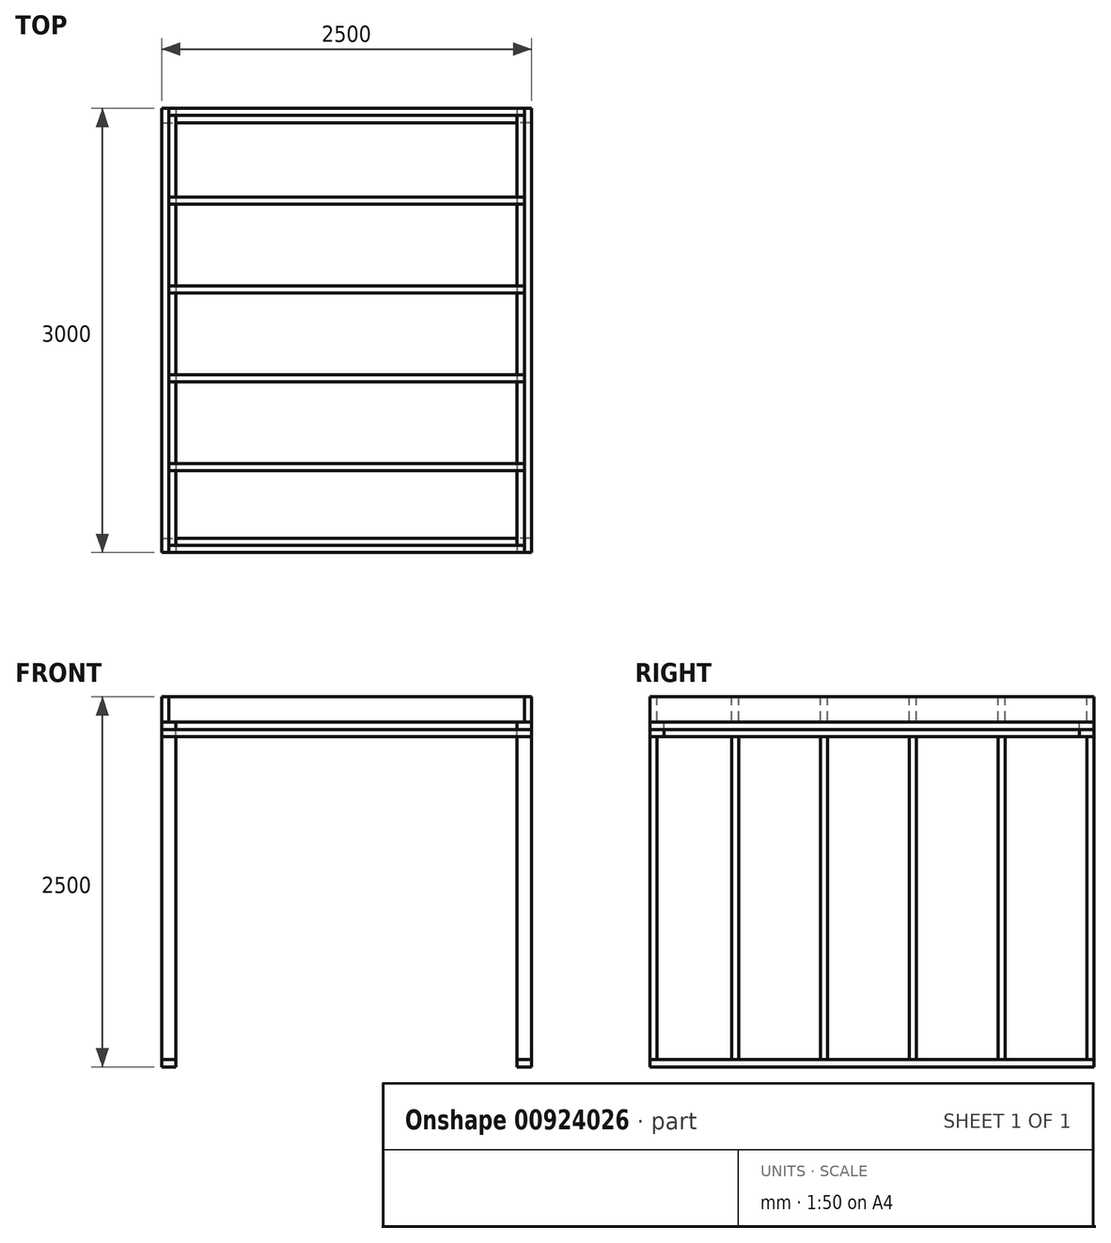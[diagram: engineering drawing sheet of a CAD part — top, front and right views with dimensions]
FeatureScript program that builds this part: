
annotation { "Feature Type Name" : "Feature", "Feature Type Description" : "" }
export const myFeature = defineFeature(function(context is Context, id is Id, definition is map)
    precondition{}
    {
        {
            assignVariable(context, id + "F0", {"name" : "poikkiparrun_korkeus", "anyValue" : 172});
        }
        {
            assignVariable(context, id + "F1", {"name" : "koolauspuun_paksuus", "anyValue" : 48});
        }
        {
            assignVariable(context, id + "F2", {"name" : "koolauspuun_korkeus", "anyValue" : 97});
        }
        {
            var Q0;
            Q0=qCreatedBy(makeId("Top.planeOp"),FACE);
            var sketch = newSketch(context, id + "F3", { "sketchPlane" : qUnion([Q0])});
            skLineSegment(sketch, "E0.bottom", {"start": v(0, 0) * mm, "end": v(-48, 0) * mm});
            skLineSegment(sketch, "E0.top", {"start": v(0, -3000) * mm, "end": v(-48, -3000) * mm});
            skLineSegment(sketch, "E0.left", {"start": v(0, 0) * mm, "end": v(0, -3000) * mm});
            skLineSegment(sketch, "E0.right", {"start": v(-48, 0) * mm, "end": v(-48, -3000) * mm});
            skLineSegment(sketch, "E1.bottom", {"start": v(-2452, 0) * mm, "end": v(-2500, 0) * mm});
            skLineSegment(sketch, "E1.top", {"start": v(-2452, -3000) * mm, "end": v(-2500, -3000) * mm});
            skLineSegment(sketch, "E1.left", {"start": v(-2452, 0) * mm, "end": v(-2452, -3000) * mm});
            skLineSegment(sketch, "E1.right", {"start": v(-2500, 0) * mm, "end": v(-2500, -3000) * mm});
            skSolve(sketch);
        }
        {
            var Q0;
            Q0 = qSketchRegion(id + "F3", true);
            extrude(context, id + "F4", {"entities" : qUnion([Q0]), "oppositeDirection" : true, "depth" : (getVariable(context, 'poikkiparrun_korkeus')) * mm, "offsetDistance" : 25 * mm});
        }
        {
            var Q0;
            Q0=makeQuery(id+"F4.opExtrude","CAP_FACE",FACE,{"disambiguationData":[OSD([sQuery(id+"F3.wireOp",EDGE,"E0.bottom"),sQuery(id+"F3.wireOp",EDGE,"E0.top"),sQuery(id+"F3.wireOp",EDGE,"E0.left"),sQuery(id+"F3.wireOp",EDGE,"E0.right")])],"isStart":true});
            var sketch = newSketch(context, id + "F5", { "sketchPlane" : qUnion([Q0])});
            skLineSegment(sketch, "E2.bottom", {"start": v(-48, 0) * mm, "end": v(-2452, 0) * mm});
            skLineSegment(sketch, "E2.top", {"start": v(-48, -48) * mm, "end": v(-2452, -48) * mm});
            skLineSegment(sketch, "E2.left", {"start": v(-48, 0) * mm, "end": v(-48, -48) * mm});
            skLineSegment(sketch, "E2.right", {"start": v(-2452, 0) * mm, "end": v(-2452, -48) * mm});
            skLineSegment(sketch, "E3.0.1.0", {"start": v(-48, -648) * mm, "end": v(-2452, -648) * mm});
            skLineSegment(sketch, "E3.0.1.1", {"start": v(-48, -600) * mm, "end": v(-2452, -600) * mm});
            skLineSegment(sketch, "E3.0.1.2", {"start": v(-2452, -600) * mm, "end": v(-2452, -648) * mm});
            skLineSegment(sketch, "E3.0.1.3", {"start": v(-48, -600) * mm, "end": v(-48, -648) * mm});
            skLineSegment(sketch, "E3.direction1", {"start": v(-2452, -48) * mm, "end": v(-1872, -48) * mm, "construction": true});
            skLineSegment(sketch, "E3.direction2", {"start": v(-2452, -48) * mm, "end": v(-2452, -648) * mm, "construction": true});
            skLineSegment(sketch, "E4.0.0.2", {"start": v(-48, -1248) * mm, "end": v(-2452, -1248) * mm});
            skLineSegment(sketch, "E4.3.0.2", {"start": v(-48, -1200) * mm, "end": v(-2452, -1200) * mm});
            skLineSegment(sketch, "E4.6.0.2", {"start": v(-2452, -1200) * mm, "end": v(-2452, -1248) * mm});
            skLineSegment(sketch, "E4.9.0.2", {"start": v(-48, -1200) * mm, "end": v(-48, -1248) * mm});
            skLineSegment(sketch, "E4.0.0.3", {"start": v(-48, -1848) * mm, "end": v(-2452, -1848) * mm});
            skLineSegment(sketch, "E4.3.0.3", {"start": v(-48, -1800) * mm, "end": v(-2452, -1800) * mm});
            skLineSegment(sketch, "E4.6.0.3", {"start": v(-2452, -1800) * mm, "end": v(-2452, -1848) * mm});
            skLineSegment(sketch, "E4.9.0.3", {"start": v(-48, -1800) * mm, "end": v(-48, -1848) * mm});
            skLineSegment(sketch, "E4.0.0.4", {"start": v(-48, -2448) * mm, "end": v(-2452, -2448) * mm});
            skLineSegment(sketch, "E4.3.0.4", {"start": v(-48, -2400) * mm, "end": v(-2452, -2400) * mm});
            skLineSegment(sketch, "E4.6.0.4", {"start": v(-2452, -2400) * mm, "end": v(-2452, -2448) * mm});
            skLineSegment(sketch, "E4.9.0.4", {"start": v(-48, -2400) * mm, "end": v(-48, -2448) * mm});
            skLineSegment(sketch, "E5.bottom", {"start": v(-48, -3000) * mm, "end": v(-2452, -3000) * mm});
            skLineSegment(sketch, "E5.top", {"start": v(-48, -2952) * mm, "end": v(-2452, -2952) * mm});
            skLineSegment(sketch, "E5.left", {"start": v(-48, -3000) * mm, "end": v(-48, -2952) * mm});
            skLineSegment(sketch, "E5.right", {"start": v(-2452, -3000) * mm, "end": v(-2452, -2952) * mm});
            skSolve(sketch);
        }
        {
            var Q0;
            Q0 = qSketchRegion(id + "F5", true);
            extrude(context, id + "F6", {"entities" : qUnion([Q0]), "oppositeDirection" : true, "depth" : (getVariable(context, 'poikkiparrun_korkeus')) * mm, "offsetDistance" : 25 * mm});
        }
        {
            var Q0;
            Q0=makeQuery(id+"F4.opExtrude","CAP_FACE",FACE,{"disambiguationData":[OSD([sQuery(id+"F3.wireOp",EDGE,"E0.bottom"),sQuery(id+"F3.wireOp",EDGE,"E0.top"),sQuery(id+"F3.wireOp",EDGE,"E0.left"),sQuery(id+"F3.wireOp",EDGE,"E0.right")])],"isStart":false});
            var sketch = newSketch(context, id + "F7", { "sketchPlane" : qUnion([Q0])});
            skLineSegment(sketch, "E6.bottom", {"start": v(0, 0) * mm, "end": v(-97, 0) * mm});
            skLineSegment(sketch, "E6.top", {"start": v(0, 3000) * mm, "end": v(-97, 3000) * mm});
            skLineSegment(sketch, "E6.left", {"start": v(0, 0) * mm, "end": v(0, 3000) * mm});
            skLineSegment(sketch, "E6.right", {"start": v(-97, 0) * mm, "end": v(-97, 3000) * mm});
            skLineSegment(sketch, "E7.bottom", {"start": v(-2500, 0) * mm, "end": v(-2403, 0) * mm});
            skLineSegment(sketch, "E7.top", {"start": v(-2500, 3000) * mm, "end": v(-2403, 3000) * mm});
            skLineSegment(sketch, "E7.left", {"start": v(-2500, 0) * mm, "end": v(-2500, 3000) * mm});
            skLineSegment(sketch, "E7.right", {"start": v(-2403, 0) * mm, "end": v(-2403, 3000) * mm});
            skSolve(sketch);
        }
        {
            var Q0;
            Q0 = qSketchRegion(id + "F7", true);
            extrude(context, id + "F8", {"entities" : qUnion([Q0]), "depth" : (getVariable(context, 'koolauspuun_paksuus')) * mm, "offsetDistance" : 25 * mm});
        }
        {
            var Q0;
            Q0=makeQuery(id+"F6.opExtrude","CAP_FACE",FACE,{"disambiguationData":[OSD([sQuery(id+"F5.wireOp",EDGE,"E2.bottom"),sQuery(id+"F5.wireOp",EDGE,"E2.top"),sQuery(id+"F5.wireOp",EDGE,"E2.left"),sQuery(id+"F5.wireOp",EDGE,"E2.right")])],"isStart":false});
            var sketch = newSketch(context, id + "F9", { "sketchPlane" : qUnion([Q0])});
            skLineSegment(sketch, "E8.bottom", {"start": v(-2403, 0) * mm, "end": v(-97, 0) * mm});
            skLineSegment(sketch, "E8.top", {"start": v(-2403, 97) * mm, "end": v(-97, 97) * mm});
            skLineSegment(sketch, "E8.left", {"start": v(-2403, 0) * mm, "end": v(-2403, 97) * mm});
            skLineSegment(sketch, "E8.right", {"start": v(-97, 0) * mm, "end": v(-97, 97) * mm});
            skLineSegment(sketch, "E9.bottom", {"start": v(-97, 3000) * mm, "end": v(-2403, 3000) * mm});
            skLineSegment(sketch, "E9.top", {"start": v(-97, 2903) * mm, "end": v(-2403, 2903) * mm});
            skLineSegment(sketch, "E9.left", {"start": v(-97, 3000) * mm, "end": v(-97, 2903) * mm});
            skLineSegment(sketch, "E9.right", {"start": v(-2403, 3000) * mm, "end": v(-2403, 2903) * mm});
            skSolve(sketch);
        }
        {
            var Q0;
            Q0 = qSketchRegion(id + "F9", true);
            extrude(context, id + "F10", {"entities" : qUnion([Q0]), "depth" : (getVariable(context, 'koolauspuun_paksuus')) * mm, "offsetDistance" : 25 * mm});
        }
        {
            var Q0;
            Q0=makeQuery(id+"F8.opExtrude","CAP_FACE",FACE,{"disambiguationData":[OSD([sQuery(id+"F7.wireOp",EDGE,"E7.bottom"),sQuery(id+"F7.wireOp",EDGE,"E7.top"),sQuery(id+"F7.wireOp",EDGE,"E7.left"),sQuery(id+"F7.wireOp",EDGE,"E7.right")])],"isStart":false});
            var sketch = newSketch(context, id + "F11", { "sketchPlane" : qUnion([Q0])});
            skLineSegment(sketch, "E10.bottom", {"start": v(-2500, 0) * mm, "end": v(0, 0) * mm});
            skLineSegment(sketch, "E10.top", {"start": v(-2500, 97) * mm, "end": v(0, 97) * mm});
            skLineSegment(sketch, "E10.left", {"start": v(-2500, 0) * mm, "end": v(-2500, 97) * mm});
            skLineSegment(sketch, "E10.right", {"start": v(0, 0) * mm, "end": v(0, 97) * mm});
            skLineSegment(sketch, "E11.bottom", {"start": v(0, 3000) * mm, "end": v(-2500, 3000) * mm});
            skLineSegment(sketch, "E11.top", {"start": v(0, 2903) * mm, "end": v(-2500, 2903) * mm});
            skLineSegment(sketch, "E11.left", {"start": v(0, 3000) * mm, "end": v(0, 2903) * mm});
            skLineSegment(sketch, "E11.right", {"start": v(-2500, 3000) * mm, "end": v(-2500, 2903) * mm});
            skSolve(sketch);
        }
        {
            var Q0;
            Q0 = qSketchRegion(id + "F11", true);
            extrude(context, id + "F12", {"entities" : qUnion([Q0]), "depth" : (getVariable(context, 'koolauspuun_paksuus')) * mm, "offsetDistance" : 25 * mm});
        }
        {
            var Q0;
            Q0=makeQuery(id+"F8.opExtrude","CAP_FACE",FACE,{"disambiguationData":[OSD([sQuery(id+"F7.wireOp",EDGE,"E6.bottom"),sQuery(id+"F7.wireOp",EDGE,"E6.top"),sQuery(id+"F7.wireOp",EDGE,"E6.left"),sQuery(id+"F7.wireOp",EDGE,"E6.right")])],"isStart":false});
            var sketch = newSketch(context, id + "F13", { "sketchPlane" : qUnion([Q0])});
            skLineSegment(sketch, "E12.bottom", {"start": v(0, 2903) * mm, "end": v(-97, 2903) * mm});
            skLineSegment(sketch, "E12.top", {"start": v(0, 97) * mm, "end": v(-97, 97) * mm});
            skLineSegment(sketch, "E12.left", {"start": v(0, 2903) * mm, "end": v(0, 97) * mm});
            skLineSegment(sketch, "E12.right", {"start": v(-97, 2903) * mm, "end": v(-97, 97) * mm});
            skLineSegment(sketch, "E13.bottom", {"start": v(-2500, 2903) * mm, "end": v(-2403, 2903) * mm});
            skLineSegment(sketch, "E13.top", {"start": v(-2500, 97) * mm, "end": v(-2403, 97) * mm});
            skLineSegment(sketch, "E13.left", {"start": v(-2500, 2903) * mm, "end": v(-2500, 97) * mm});
            skLineSegment(sketch, "E13.right", {"start": v(-2403, 2903) * mm, "end": v(-2403, 97) * mm});
            skSolve(sketch);
        }
        {
            var Q0;
            Q0 = qSketchRegion(id + "F13", true);
            extrude(context, id + "F14", {"entities" : qUnion([Q0]), "depth" : (getVariable(context, 'koolauspuun_paksuus')) * mm, "offsetDistance" : 25 * mm});
        }
        {
            var Q0;
            Q0=qCreatedBy(makeId("Right.planeOp"),FACE);
            var sketch = newSketch(context, id + "F15", { "sketchPlane" : qUnion([Q0])});
            skLineSegment(sketch, "E14.bottom", {"start": v(0, -2500) * mm, "end": v(-3000, -2500) * mm});
            skLineSegment(sketch, "E14.top", {"start": v(0, -2452) * mm, "end": v(-3000, -2452) * mm});
            skLineSegment(sketch, "E14.left", {"start": v(0, -2500) * mm, "end": v(0, -2452) * mm});
            skLineSegment(sketch, "E14.right", {"start": v(-3000, -2500) * mm, "end": v(-3000, -2452) * mm});
            skSolve(sketch);
        }
        {
            var Q0;
            Q0 = qSketchRegion(id + "F15", true);
            extrude(context, id + "F16", {"entities" : qUnion([Q0]), "oppositeDirection" : true, "depth" : (getVariable(context, 'koolauspuun_korkeus')) * mm, "offsetDistance" : 25 * mm});
        }
        {
            var Q0;
            Q0=qCreatedBy(makeId("Right.planeOp"),FACE);
            var sketch = newSketch(context, id + "F17", { "sketchPlane" : qUnion([Q0])});
            skLineSegment(sketch, "E15.bottom", {"start": v(0, -268) * mm, "end": v(-48, -268) * mm});
            skLineSegment(sketch, "E15.top", {"start": v(0, -2452) * mm, "end": v(-48, -2452) * mm});
            skLineSegment(sketch, "E15.left", {"start": v(0, -268) * mm, "end": v(0, -2452) * mm});
            skLineSegment(sketch, "E15.right", {"start": v(-48, -268) * mm, "end": v(-48, -2452) * mm});
            skLineSegment(sketch, "E16.1.0.0", {"start": v(-648, -268) * mm, "end": v(-648, -2452) * mm});
            skLineSegment(sketch, "E16.1.0.1", {"start": v(-600, -268) * mm, "end": v(-600, -2452) * mm});
            skLineSegment(sketch, "E16.1.0.2", {"start": v(-600, -268) * mm, "end": v(-648, -268) * mm});
            skLineSegment(sketch, "E16.1.0.3", {"start": v(-600, -2452) * mm, "end": v(-648, -2452) * mm});
            skLineSegment(sketch, "E16.2.0.0", {"start": v(-1248, -268) * mm, "end": v(-1248, -2452) * mm});
            skLineSegment(sketch, "E16.2.0.1", {"start": v(-1200, -268) * mm, "end": v(-1200, -2452) * mm});
            skLineSegment(sketch, "E16.2.0.2", {"start": v(-1200, -268) * mm, "end": v(-1248, -268) * mm});
            skLineSegment(sketch, "E16.2.0.3", {"start": v(-1200, -2452) * mm, "end": v(-1248, -2452) * mm});
            skLineSegment(sketch, "E16.3.0.0", {"start": v(-1848, -268) * mm, "end": v(-1848, -2452) * mm});
            skLineSegment(sketch, "E16.3.0.1", {"start": v(-1800, -268) * mm, "end": v(-1800, -2452) * mm});
            skLineSegment(sketch, "E16.3.0.2", {"start": v(-1800, -268) * mm, "end": v(-1848, -268) * mm});
            skLineSegment(sketch, "E16.3.0.3", {"start": v(-1800, -2452) * mm, "end": v(-1848, -2452) * mm});
            skLineSegment(sketch, "E16.4.0.0", {"start": v(-2448, -268) * mm, "end": v(-2448, -2452) * mm});
            skLineSegment(sketch, "E16.4.0.1", {"start": v(-2400, -268) * mm, "end": v(-2400, -2452) * mm});
            skLineSegment(sketch, "E16.4.0.2", {"start": v(-2400, -268) * mm, "end": v(-2448, -268) * mm});
            skLineSegment(sketch, "E16.4.0.3", {"start": v(-2400, -2452) * mm, "end": v(-2448, -2452) * mm});
            skLineSegment(sketch, "E16.direction1", {"start": v(-48, -2452) * mm, "end": v(-648, -2452) * mm, "construction": true});
            skLineSegment(sketch, "E17.bottom", {"start": v(-3000, -268) * mm, "end": v(-2952, -268) * mm});
            skLineSegment(sketch, "E17.top", {"start": v(-3000, -2452) * mm, "end": v(-2952, -2452) * mm});
            skLineSegment(sketch, "E17.left", {"start": v(-3000, -268) * mm, "end": v(-3000, -2452) * mm});
            skLineSegment(sketch, "E17.right", {"start": v(-2952, -268) * mm, "end": v(-2952, -2452) * mm});
            skSolve(sketch);
        }
        {
            var Q0;
            Q0 = qSketchRegion(id + "F17", true);
            extrude(context, id + "F18", {"entities" : qUnion([Q0]), "oppositeDirection" : true, "depth" : (getVariable(context, 'koolauspuun_korkeus')) * mm, "offsetDistance" : 25 * mm});
        }
        {
            var Q0;
            Q0=makeQuery(id+"F4.opExtrude","SWEPT_FACE",FACE,{"disambiguationData":[OSD([sQuery(id+"F3.wireOp",EDGE,"E1.right")])]});
            var sketch = newSketch(context, id + "F19", { "sketchPlane" : qUnion([Q0])});
            skLineSegment(sketch, "E18.bottom", {"start": v(0, -2500) * mm, "end": v(3000, -2500) * mm});
            skLineSegment(sketch, "E18.top", {"start": v(0, -2452) * mm, "end": v(3000, -2452) * mm});
            skLineSegment(sketch, "E18.left", {"start": v(0, -2500) * mm, "end": v(0, -2452) * mm});
            skLineSegment(sketch, "E18.right", {"start": v(3000, -2500) * mm, "end": v(3000, -2452) * mm});
            skSolve(sketch);
        }
        {
            var Q0;
            Q0 = qSketchRegion(id + "F19", true);
            extrude(context, id + "F20", {"entities" : qUnion([Q0]), "oppositeDirection" : true, "depth" : (getVariable(context, 'koolauspuun_korkeus')) * mm, "offsetDistance" : 25 * mm});
        }
        {
            var Q0;
            Q0=makeQuery(id+"F4.opExtrude","SWEPT_FACE",FACE,{"disambiguationData":[OSD([sQuery(id+"F3.wireOp",EDGE,"E1.right")])]});
            var sketch = newSketch(context, id + "F21", { "sketchPlane" : qUnion([Q0])});
            skLineSegment(sketch, "E19.bottom", {"start": v(0, -268) * mm, "end": v(48, -268) * mm});
            skLineSegment(sketch, "E19.top", {"start": v(0, -2452) * mm, "end": v(48, -2452) * mm});
            skLineSegment(sketch, "E19.left", {"start": v(0, -268) * mm, "end": v(0, -2452) * mm});
            skLineSegment(sketch, "E19.right", {"start": v(48, -268) * mm, "end": v(48, -2452) * mm});
            skLineSegment(sketch, "E20.1.0.0", {"start": v(648, -268) * mm, "end": v(648, -2452) * mm});
            skLineSegment(sketch, "E20.1.0.1", {"start": v(600, -268) * mm, "end": v(600, -2452) * mm});
            skLineSegment(sketch, "E20.1.0.2", {"start": v(600, -2452) * mm, "end": v(648, -2452) * mm});
            skLineSegment(sketch, "E20.1.0.3", {"start": v(600, -268) * mm, "end": v(648, -268) * mm});
            skLineSegment(sketch, "E20.direction1", {"start": v(0, -2452) * mm, "end": v(600, -2452) * mm, "construction": true});
            skSolve(sketch);
        }
        {
            var Q0;
            Q0 = qSketchRegion(id + "F21", true);
            extrude(context, id + "F22", {"entities" : qUnion([Q0]), "oppositeDirection" : true, "depth" : (getVariable(context, 'koolauspuun_korkeus')) * mm, "offsetDistance" : 25 * mm});
        }
        {
            var Q0;
            Q0=makeQuery(id+"F4.opExtrude","SWEPT_FACE",FACE,{"disambiguationData":[OSD([sQuery(id+"F3.wireOp",EDGE,"E1.right")])]});
            var sketch = newSketch(context, id + "F23", { "sketchPlane" : qUnion([Q0])});
            skLineSegment(sketch, "E21.bottom", {"start": v(3000, -268) * mm, "end": v(2952, -268) * mm});
            skLineSegment(sketch, "E21.top", {"start": v(3000, -2452) * mm, "end": v(2952, -2452) * mm});
            skLineSegment(sketch, "E21.left", {"start": v(3000, -268) * mm, "end": v(3000, -2452) * mm});
            skLineSegment(sketch, "E21.right", {"start": v(2952, -268) * mm, "end": v(2952, -2452) * mm});
            skSolve(sketch);
        }
        {
            var Q0;
            Q0 = qSketchRegion(id + "F23", true);
            extrude(context, id + "F24", {"entities" : qUnion([Q0]), "oppositeDirection" : true, "depth" : (getVariable(context, 'koolauspuun_korkeus')) * mm, "offsetDistance" : 25 * mm});
        }
    });
